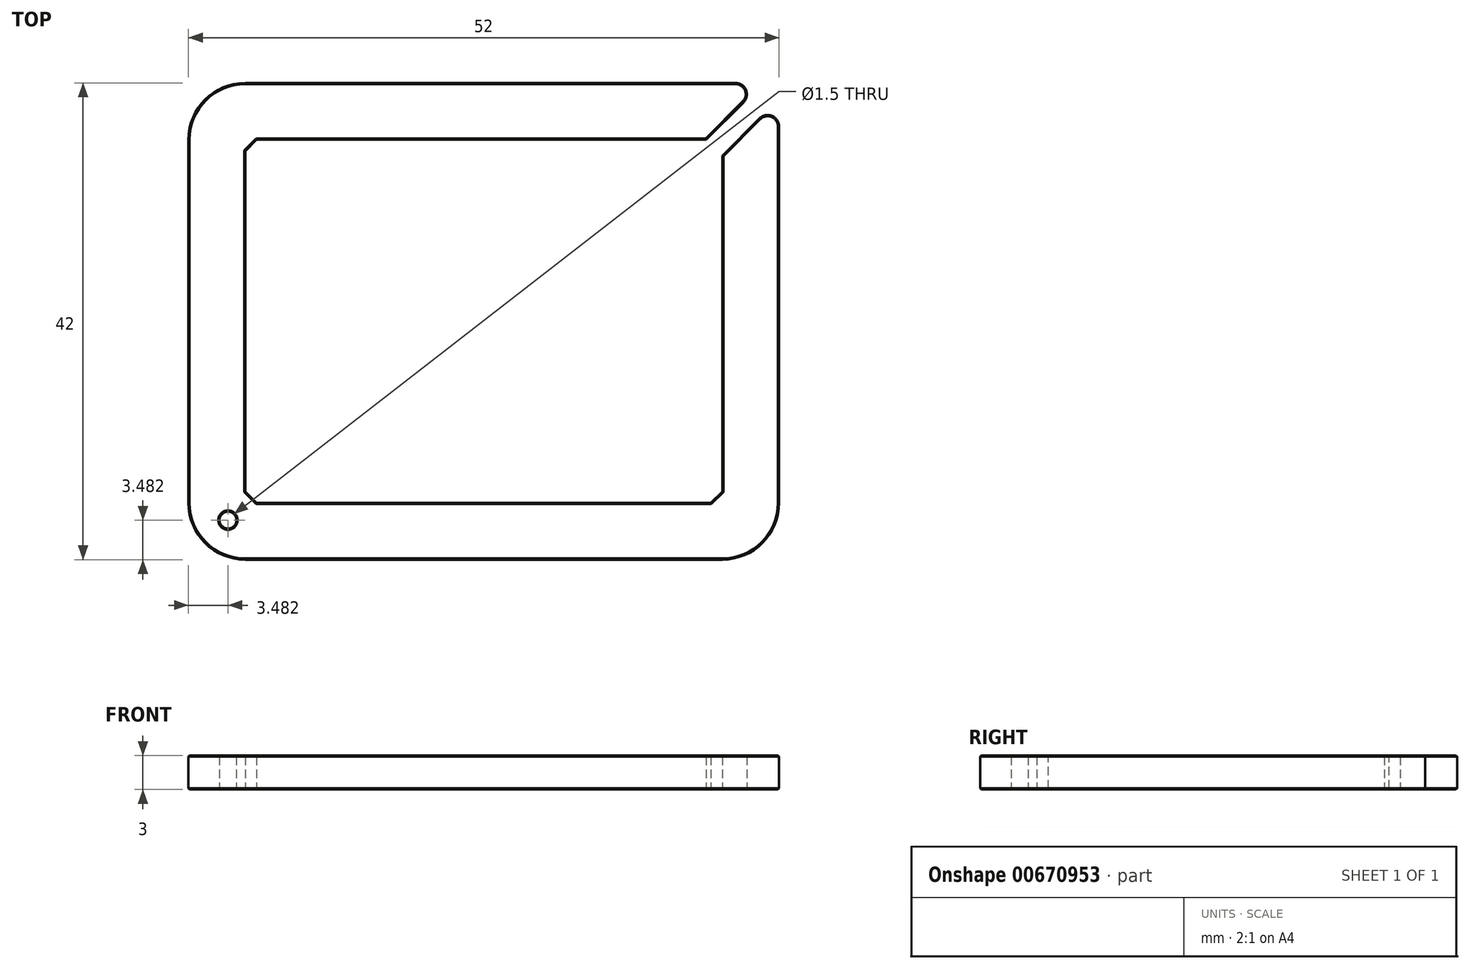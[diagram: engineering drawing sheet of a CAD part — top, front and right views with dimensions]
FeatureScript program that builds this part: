
annotation { "Feature Type Name" : "Feature", "Feature Type Description" : "" }
export const myFeature = defineFeature(function(context is Context, id is Id, definition is map)
    precondition{}
    {
        {
            var Q0;
            Q0=qCreatedBy(makeId("Top.planeOp"),FACE);
            var sketch = newSketch(context, id + "F0", { "sketchPlane" : qUnion([Q0])});
            skLineSegment(sketch, "E0.bottom", {"start": v(-26, 21) * mm, "end": v(24.59, 21) * mm});
            skLineSegment(sketch, "E0.top", {"start": v(-26, -21) * mm, "end": v(26, -21) * mm});
            skLineSegment(sketch, "E0.left", {"start": v(-26, 21) * mm, "end": v(-26, -21) * mm});
            skLineSegment(sketch, "E0.right", {"start": v(26, 19.59) * mm, "end": v(26, -21) * mm});
            skPoint(sketch, "E0.middle", {"position": v(0, 0) * mm});
            skLineSegment(sketch, "E1.bottom", {"start": v(-21, 16) * mm, "end": v(19.59, 16) * mm});
            skLineSegment(sketch, "E1.top", {"start": v(-20, -16) * mm, "end": v(21, -16) * mm});
            skLineSegment(sketch, "E1.left", {"start": v(-21, 16) * mm, "end": v(-21, -15) * mm});
            skLineSegment(sketch, "E1.right", {"start": v(21, 14.59) * mm, "end": v(21, -16) * mm});
            skLineSegment(sketch, "E2", {"start": v(26, 19.59) * mm, "end": v(21, 14.59) * mm});
            skLineSegment(sketch, "E3", {"start": v(24.59, 21) * mm, "end": v(19.59, 16) * mm});
            skLineSegment(sketch, "E4", {"start": v(-21, -15) * mm, "end": v(-20, -16) * mm});
            skCircle(sketch, "E5", {"center": v(-22.52, -17.52) * mm, "radius": 0.75 * mm});
            skPoint(sketch, "E6.end.orphan", {"position": v(-20.5, -15.5) * mm});
            skSolve(sketch);
        }
        {
            var Q0;
            Q0=makeQuery(id+"F0.imprint","IMPRINT",FACE,{"disambiguationData":[TD([[makeQuery(id+"F0.imprint","IMPRINT",EDGE,{"derivedFrom":sQuery(id+"F0.wireOp",EDGE,"E0.bottom")}),-1.0]])]});
            var Q1;
            {var subQ5=sQuery(id+"F0.wireOp",EDGE,"E0.top");Q1=makeQuery(id+"F0.imprint","IMPRINT",FACE,{"disambiguationData":[TD([[makeQuery(id+"F0.imprint","IMPRINT",EDGE,{"derivedFrom":subQ5}),1.0]])]});}
            extrude(context, id + "F1", {"entities" : qUnion([Q0, Q1]), "depth" : 3 * mm, "offsetDistance" : 25 * mm});
        }
        {
            var Q0;
            Q0=makeQuery(id+"F1.opExtrude","SWEPT_EDGE",EDGE,{"disambiguationData":[OSD([sQuery(id+"F0.wireOp",EDGE,"E0.bottom"),sQuery(id+"F0.wireOp",EDGE,"E0.left")])]});
            var Q1;
            Q1=makeQuery(id+"F1.opExtrude","SWEPT_EDGE",EDGE,{"disambiguationData":[OSD([sQuery(id+"F0.wireOp",EDGE,"E0.top"),sQuery(id+"F0.wireOp",EDGE,"E0.right")])]});
            var Q2;
            Q2=makeQuery(id+"F1.opExtrude","SWEPT_EDGE",EDGE,{"disambiguationData":[OSD([sQuery(id+"F0.wireOp",EDGE,"E0.top"),sQuery(id+"F0.wireOp",EDGE,"E0.left")])]});
            fillet(context, id + "F2", {"entities" : qUnion([Q0, Q1, Q2]), "radius" : 5 * mm, "tangentPropagation" : true, "allowEdgeOverflow" : false});
        }
        {
            var Q0;
            Q0=makeQuery(id+"F1.opExtrude","SWEPT_EDGE",EDGE,{"disambiguationData":[OSD([sQuery(id+"F0.wireOp",EDGE,"E1.bottom"),sQuery(id+"F0.wireOp",EDGE,"E1.left")])]});
            var Q1;
            Q1=makeQuery(id+"F1.opExtrude","SWEPT_EDGE",EDGE,{"disambiguationData":[OSD([sQuery(id+"F0.wireOp",EDGE,"E1.top"),sQuery(id+"F0.wireOp",EDGE,"E1.right")])]});
            chamfer(context, id + "F3", {"entities" : qUnion([Q0, Q1]), "chamferType" : ChamferType.TWO_OFFSETS, "width1" : 1 * mm, "oppositeDirection" : true, "width2" : 1 * mm, "tangentPropagation" : true});
        }
        {
            var Q0;
            Q0=makeQuery(id+"F1.opExtrude","CAP_FACE",FACE,{"disambiguationData":[OSD([sQuery(id+"F0.wireOp",EDGE,"E0.bottom"),sQuery(id+"F0.wireOp",EDGE,"E0.top"),sQuery(id+"F0.wireOp",EDGE,"E0.left"),sQuery(id+"F0.wireOp",EDGE,"E0.right"),sQuery(id+"F0.wireOp",EDGE,"E1.bottom"),sQuery(id+"F0.wireOp",EDGE,"E1.top"),sQuery(id+"F0.wireOp",EDGE,"E1.left"),sQuery(id+"F0.wireOp",EDGE,"E1.right")])],"isStart":false});
            var Q1;
            Q1=makeQuery(id+"F1.opExtrude","CAP_FACE",FACE,{"disambiguationData":[OSD([sQuery(id+"F0.wireOp",EDGE,"E0.bottom"),sQuery(id+"F0.wireOp",EDGE,"E0.top"),sQuery(id+"F0.wireOp",EDGE,"E0.left"),sQuery(id+"F0.wireOp",EDGE,"E0.right"),sQuery(id+"F0.wireOp",EDGE,"E1.bottom"),sQuery(id+"F0.wireOp",EDGE,"E1.top"),sQuery(id+"F0.wireOp",EDGE,"E1.left"),sQuery(id+"F0.wireOp",EDGE,"E1.right")])],"isStart":true});
            chamfer(context, id + "F4", {"entities" : qUnion([Q0, Q1]), "width" : 0.1 * mm, "tangentPropagation" : true});
        }
        {
            var Q0;
            Q0=makeQuery(id+"F1.opExtrude","SWEPT_EDGE",EDGE,{"disambiguationData":[OSD([sQuery(id+"F0.wireOp",EDGE,"E0.right"),sQuery(id+"F0.wireOp",EDGE,"E2")])]});
            var Q1;
            Q1=makeQuery(id+"F1.opExtrude","SWEPT_EDGE",EDGE,{"disambiguationData":[OSD([sQuery(id+"F0.wireOp",EDGE,"E0.bottom"),sQuery(id+"F0.wireOp",EDGE,"E3")])]});
            fillet(context, id + "F5", {"entities" : qUnion([Q0, Q1]), "radius" : 1 * mm, "tangentPropagation" : true, "allowEdgeOverflow" : false});
        }
        {
            var Q0;
            {var subQ0=sQuery(id+"F0.wireOp",EDGE,"E2");var subQ1=sQuery(id+"F0.wireOp",EDGE,"E0.right");Q0=makeQuery(id+"F5.opFillet","BLEND_EDGE",EDGE,{"blendedFrom":[makeQuery(id+"F1.opExtrude","SWEPT_EDGE",EDGE,{"disambiguationData":[OSD([subQ1,subQ0])]}),makeQuery(id+"F1.opExtrude","CAP_FACE",FACE,{"disambiguationData":[OSD([sQuery(id+"F0.wireOp",EDGE,"E0.bottom"),sQuery(id+"F0.wireOp",EDGE,"E0.top"),sQuery(id+"F0.wireOp",EDGE,"E0.left"),subQ1,sQuery(id+"F0.wireOp",EDGE,"E1.bottom"),sQuery(id+"F0.wireOp",EDGE,"E1.top"),sQuery(id+"F0.wireOp",EDGE,"E1.left"),sQuery(id+"F0.wireOp",EDGE,"E1.right"),subQ0,sQuery(id+"F0.wireOp",EDGE,"E3"),sQuery(id+"F0.wireOp",EDGE,"E4"),sQuery(id+"F0.wireOp",EDGE,"E5")])],"isStart":false})],"blendedInto":[makeQuery(id+"F1.opExtrude","CAP_FACE",FACE,{"disambiguationData":[OSD([sQuery(id+"F0.wireOp",EDGE,"E0.bottom"),sQuery(id+"F0.wireOp",EDGE,"E0.top"),sQuery(id+"F0.wireOp",EDGE,"E0.left"),subQ1,sQuery(id+"F0.wireOp",EDGE,"E1.bottom"),sQuery(id+"F0.wireOp",EDGE,"E1.top"),sQuery(id+"F0.wireOp",EDGE,"E1.left"),sQuery(id+"F0.wireOp",EDGE,"E1.right"),subQ0,sQuery(id+"F0.wireOp",EDGE,"E3"),sQuery(id+"F0.wireOp",EDGE,"E4"),sQuery(id+"F0.wireOp",EDGE,"E5")])],"isStart":false})]});}
            var Q1;
            {var subQ0=sQuery(id+"F0.wireOp",EDGE,"E3");var subQ1=sQuery(id+"F0.wireOp",EDGE,"E0.bottom");Q1=makeQuery(id+"F5.opFillet","BLEND_EDGE",EDGE,{"blendedFrom":[makeQuery(id+"F1.opExtrude","SWEPT_EDGE",EDGE,{"disambiguationData":[OSD([subQ1,subQ0])]}),makeQuery(id+"F1.opExtrude","CAP_FACE",FACE,{"disambiguationData":[OSD([subQ1,sQuery(id+"F0.wireOp",EDGE,"E0.top"),sQuery(id+"F0.wireOp",EDGE,"E0.left"),sQuery(id+"F0.wireOp",EDGE,"E0.right"),sQuery(id+"F0.wireOp",EDGE,"E1.bottom"),sQuery(id+"F0.wireOp",EDGE,"E1.top"),sQuery(id+"F0.wireOp",EDGE,"E1.left"),sQuery(id+"F0.wireOp",EDGE,"E1.right"),sQuery(id+"F0.wireOp",EDGE,"E2"),subQ0,sQuery(id+"F0.wireOp",EDGE,"E4"),sQuery(id+"F0.wireOp",EDGE,"E5")])],"isStart":false})],"blendedInto":[makeQuery(id+"F1.opExtrude","CAP_FACE",FACE,{"disambiguationData":[OSD([subQ1,sQuery(id+"F0.wireOp",EDGE,"E0.top"),sQuery(id+"F0.wireOp",EDGE,"E0.left"),sQuery(id+"F0.wireOp",EDGE,"E0.right"),sQuery(id+"F0.wireOp",EDGE,"E1.bottom"),sQuery(id+"F0.wireOp",EDGE,"E1.top"),sQuery(id+"F0.wireOp",EDGE,"E1.left"),sQuery(id+"F0.wireOp",EDGE,"E1.right"),sQuery(id+"F0.wireOp",EDGE,"E2"),subQ0,sQuery(id+"F0.wireOp",EDGE,"E4"),sQuery(id+"F0.wireOp",EDGE,"E5")])],"isStart":false})]});}
            var Q2;
            {var subQ0=sQuery(id+"F0.wireOp",EDGE,"E3");var subQ1=sQuery(id+"F0.wireOp",EDGE,"E0.bottom");Q2=makeQuery(id+"F5.opFillet","BLEND_EDGE",EDGE,{"blendedFrom":[makeQuery(id+"F1.opExtrude","SWEPT_EDGE",EDGE,{"disambiguationData":[OSD([subQ1,subQ0])]}),makeQuery(id+"F1.opExtrude","CAP_FACE",FACE,{"disambiguationData":[OSD([subQ1,sQuery(id+"F0.wireOp",EDGE,"E0.top"),sQuery(id+"F0.wireOp",EDGE,"E0.left"),sQuery(id+"F0.wireOp",EDGE,"E0.right"),sQuery(id+"F0.wireOp",EDGE,"E1.bottom"),sQuery(id+"F0.wireOp",EDGE,"E1.top"),sQuery(id+"F0.wireOp",EDGE,"E1.left"),sQuery(id+"F0.wireOp",EDGE,"E1.right"),sQuery(id+"F0.wireOp",EDGE,"E2"),subQ0,sQuery(id+"F0.wireOp",EDGE,"E4"),sQuery(id+"F0.wireOp",EDGE,"E5")])],"isStart":true})],"blendedInto":[makeQuery(id+"F1.opExtrude","CAP_FACE",FACE,{"disambiguationData":[OSD([subQ1,sQuery(id+"F0.wireOp",EDGE,"E0.top"),sQuery(id+"F0.wireOp",EDGE,"E0.left"),sQuery(id+"F0.wireOp",EDGE,"E0.right"),sQuery(id+"F0.wireOp",EDGE,"E1.bottom"),sQuery(id+"F0.wireOp",EDGE,"E1.top"),sQuery(id+"F0.wireOp",EDGE,"E1.left"),sQuery(id+"F0.wireOp",EDGE,"E1.right"),sQuery(id+"F0.wireOp",EDGE,"E2"),subQ0,sQuery(id+"F0.wireOp",EDGE,"E4"),sQuery(id+"F0.wireOp",EDGE,"E5")])],"isStart":true})]});}
            var Q3;
            {var subQ0=sQuery(id+"F0.wireOp",EDGE,"E2");var subQ1=sQuery(id+"F0.wireOp",EDGE,"E0.right");Q3=makeQuery(id+"F5.opFillet","BLEND_EDGE",EDGE,{"blendedFrom":[makeQuery(id+"F1.opExtrude","SWEPT_EDGE",EDGE,{"disambiguationData":[OSD([subQ1,subQ0])]}),makeQuery(id+"F1.opExtrude","CAP_FACE",FACE,{"disambiguationData":[OSD([sQuery(id+"F0.wireOp",EDGE,"E0.bottom"),sQuery(id+"F0.wireOp",EDGE,"E0.top"),sQuery(id+"F0.wireOp",EDGE,"E0.left"),subQ1,sQuery(id+"F0.wireOp",EDGE,"E1.bottom"),sQuery(id+"F0.wireOp",EDGE,"E1.top"),sQuery(id+"F0.wireOp",EDGE,"E1.left"),sQuery(id+"F0.wireOp",EDGE,"E1.right"),subQ0,sQuery(id+"F0.wireOp",EDGE,"E3"),sQuery(id+"F0.wireOp",EDGE,"E4"),sQuery(id+"F0.wireOp",EDGE,"E5")])],"isStart":true})],"blendedInto":[makeQuery(id+"F1.opExtrude","CAP_FACE",FACE,{"disambiguationData":[OSD([sQuery(id+"F0.wireOp",EDGE,"E0.bottom"),sQuery(id+"F0.wireOp",EDGE,"E0.top"),sQuery(id+"F0.wireOp",EDGE,"E0.left"),subQ1,sQuery(id+"F0.wireOp",EDGE,"E1.bottom"),sQuery(id+"F0.wireOp",EDGE,"E1.top"),sQuery(id+"F0.wireOp",EDGE,"E1.left"),sQuery(id+"F0.wireOp",EDGE,"E1.right"),subQ0,sQuery(id+"F0.wireOp",EDGE,"E3"),sQuery(id+"F0.wireOp",EDGE,"E4"),sQuery(id+"F0.wireOp",EDGE,"E5")])],"isStart":true})]});}
            chamfer(context, id + "F6", {"entities" : qUnion([Q0, Q1, Q2, Q3]), "width" : 0.1 * mm, "tangentPropagation" : true});
        }
    });
